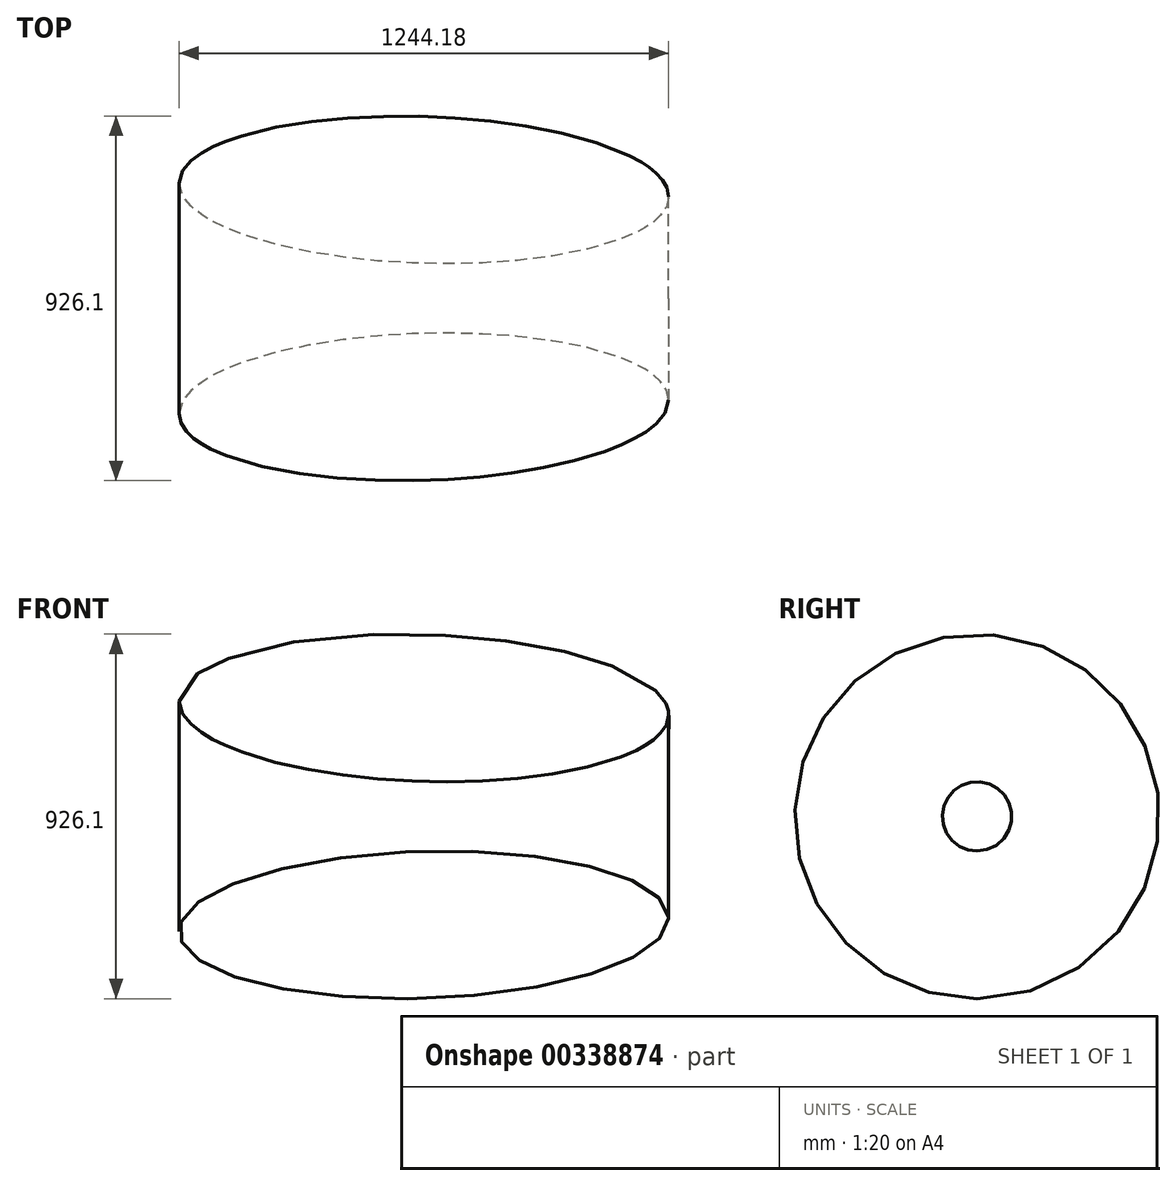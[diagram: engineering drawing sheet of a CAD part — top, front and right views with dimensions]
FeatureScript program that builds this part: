
annotation { "Feature Type Name" : "Feature", "Feature Type Description" : "" }
export const myFeature = defineFeature(function(context is Context, id is Id, definition is map)
    precondition{}
    {
        {
            var Q0;
            Q0=qCreatedBy(makeId("Front.planeOp"),FACE);
            var sketch = newSketch(context, id + "F0", { "sketchPlane" : qUnion([Q0])});
            skEllipse(sketch, "E0", {"center": v(-678.43, 86.63) * mm, "majorRadius": 622.35 * mm, "minorRadius": 186.65 * mm, "majorAxis": v(1, 0.03)});
            skLineSegment(sketch, "E1", {"start": v(-1260.83, 362.18) * mm, "end": v(45.92, 362.18) * mm, "construction": true});
            skSolve(sketch);
        }
        {
            var Q0;
            Q0=makeQuery(id+"F0.imprint","IMPRINT",FACE,{"disambiguationData":[TD([[makeQuery(id+"F0.imprint","IMPRINT",EDGE,{"derivedFrom":sQuery(id+"F0.wireOp",EDGE,"E0")}),1.0]])]});
            var Q1;
            Q1=sQuery(id+"F0.wireOp",EDGE,"E1");
            var Q2;
            Q2=sQuery(id+"F0.wireOp",EDGE,"E1");
            revolve(context, id + "F1", {"entities" : qUnion([Q0]), "surfaceEntities" : qUnion([Q1]), "axis" : qUnion([Q2]), "revolveType" : RevolveType.FULL});
        }
    });
